# Revit family: Bath-Alcove-KOHLER-BIOVE-K-99203T
name_source: partatom
category: Plumbing Fixtures
revit_build: Autodesk Revit 2017 (Build: 20160225_1515(x64)
units: mm (PartAtom-declared; Revit-internal decimal feet)

## family parameters
Cut with Voids When Loaded = No
Host = Face
OmniClass Number = 23.31.15.00
Part Type = Normal
Room Calculation Point = No
Round Connector Dimension = Use Diameter
Shared = No

## types (3) — shared parameters
ADA Compliant = No
Assembly Code = D2010500
CW Connection = No
Cold Water Inlet = Cold Water Inlet
Date Modified = 03/05/2021
Default Elevation = 0"
Description = Corner cast iron bathtub with wooden skirt (left corner)
Drain Included = No
HW Connection = No
Height = 23 1/8"
Hot Water Inlet = Hot Water Inlet
Length = 66 15/16"
Manufacturer = KOHLER Co.
Master Format 2014 = 22 41 19
Master Format 2014 Name = Residential Bathtubs
Material = Cast Iron
Product Documentation Link = https://files.kohler.com.cn
Product Name = BIOVE
Product Page URL = https://www.kohler.com.cn
URL = https://www.kohler.com.cn
Vent Connection = No
Waste Connection = Yes
Waste Water Outlet = Waste Water Outlet
WaterSense Certified = No
Width = 29 1/2"

## per-type parameters (varying)
| type | Finish | Model | Type |
| E63-Walnut | Kohler-Wood-E63-Walnut | K-99203T-E63 | 1 |
| C38-White | Kohler-Wood-C38-White | K-99203T-C38 | 2 |
| C36-Ebony | Kohler-Wood-C36-Ebony | K-99203T-C36 | 3 |

## geometry (parser evidence)
native form markers: Sweep x5
no freeform markers — native parametric forms only
